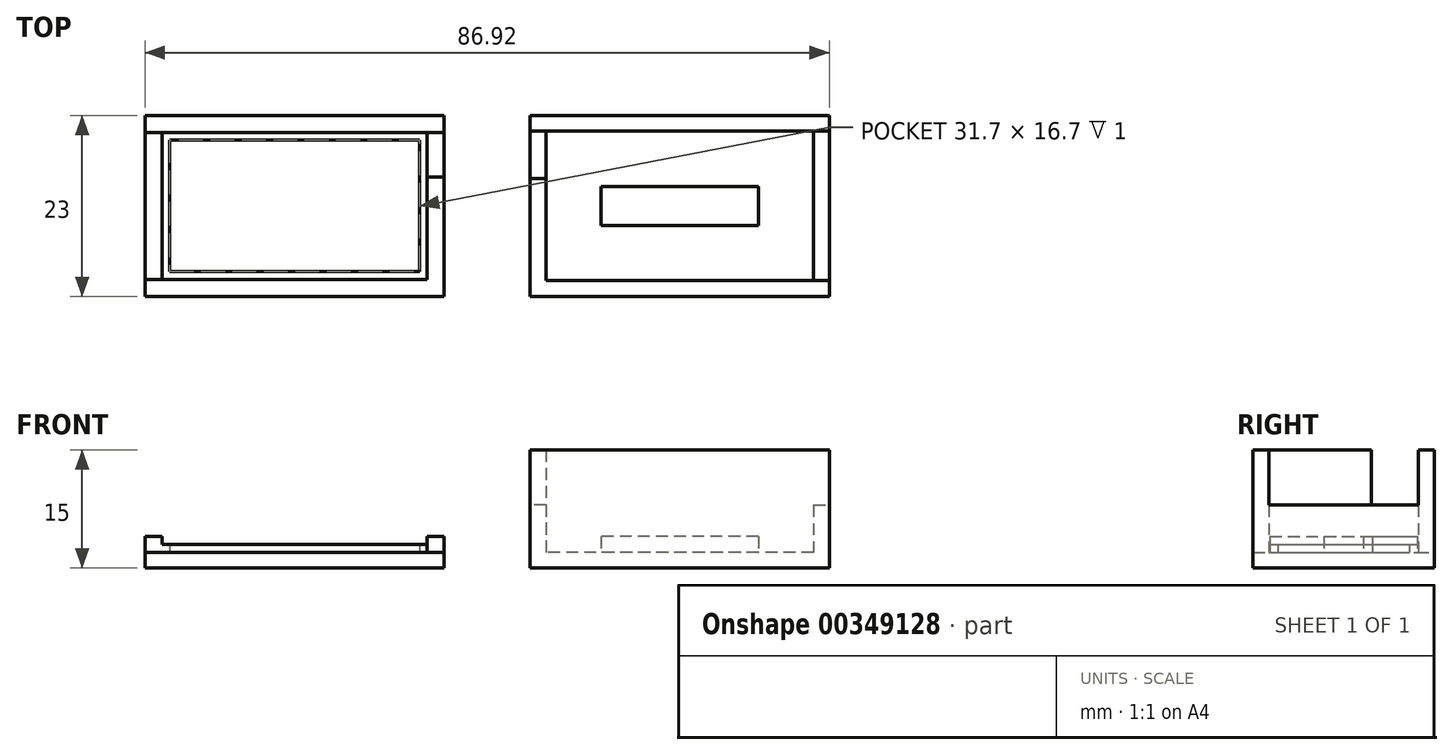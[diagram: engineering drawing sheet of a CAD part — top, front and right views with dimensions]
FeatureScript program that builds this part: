
annotation { "Feature Type Name" : "Feature", "Feature Type Description" : "" }
export const myFeature = defineFeature(function(context is Context, id is Id, definition is map)
    precondition{}
    {
        {
            var Q0;
            Q0=qCreatedBy(makeId("Top.planeOp"),FACE);
            var sketch = newSketch(context, id + "F0", { "sketchPlane" : qUnion([Q0])});
            skLineSegment(sketch, "E0.bottom", {"start": v(17, -9.5) * mm, "end": v(-17, -9.5) * mm});
            skLineSegment(sketch, "E0.top", {"start": v(17, 9.5) * mm, "end": v(-17, 9.5) * mm});
            skLineSegment(sketch, "E0.left", {"start": v(17, -9.5) * mm, "end": v(17, 9.5) * mm});
            skLineSegment(sketch, "E0.right", {"start": v(-17, -9.5) * mm, "end": v(-17, 9.5) * mm});
            skPoint(sketch, "E0.middle", {"position": v(0, 0) * mm});
            skLineSegment(sketch, "E1.bottom", {"start": v(10, -2.5) * mm, "end": v(-10, -2.5) * mm});
            skLineSegment(sketch, "E1.top", {"start": v(10, 2.5) * mm, "end": v(-10, 2.5) * mm});
            skLineSegment(sketch, "E1.left", {"start": v(10, -2.5) * mm, "end": v(10, 2.5) * mm});
            skLineSegment(sketch, "E1.right", {"start": v(-10, -2.5) * mm, "end": v(-10, 2.5) * mm});
            skLineSegment(sketch, "E2.0", {"start": v(19, 11.5) * mm, "end": v(-19, 11.5) * mm});
            skLineSegment(sketch, "E2.1", {"start": v(19, -11.5) * mm, "end": v(19, 11.5) * mm});
            skLineSegment(sketch, "E2.2", {"start": v(19, -11.5) * mm, "end": v(-19, -11.5) * mm});
            skLineSegment(sketch, "E2.3", {"start": v(-19, -11.5) * mm, "end": v(-19, 11.5) * mm});
            skLineSegment(sketch, "E3", {"start": v(17, 9.5) * mm, "end": v(19, 9.5) * mm});
            skLineSegment(sketch, "E4", {"start": v(17, -9.5) * mm, "end": v(19, -9.5) * mm});
            skLineSegment(sketch, "E5", {"start": v(-17, 9.5) * mm, "end": v(-19, 9.5) * mm});
            skLineSegment(sketch, "E6", {"start": v(-17, 3.5) * mm, "end": v(-19, 3.5) * mm});
            skSolve(sketch);
        }
        {
            var Q0;
            Q0=makeQuery(id+"F0.imprint","IMPRINT",FACE,{"disambiguationData":[TD([[makeQuery(id+"F0.imprint","IMPRINT",EDGE,{"derivedFrom":sQuery(id+"F0.wireOp",EDGE,"E0.bottom")}),-1.0]])]});
            extrude(context, id + "F1", {"entities" : qUnion([Q0]), "depth" : 2 * mm});
        }
        {
            var Q0;
            Q0=makeQuery(id+"F0.imprint","IMPRINT",FACE,{"disambiguationData":[TD([[makeQuery(id+"F0.imprint","IMPRINT",EDGE,{"derivedFrom":sQuery(id+"F0.wireOp",EDGE,"E1.bottom")}),-1.0]])]});
            extrude(context, id + "F2", {"entities" : qUnion([Q0]), "operationType" : NewBodyOperationType.ADD, "depth" : 4 * mm});
        }
        {
            var Q0;
            Q0=makeQuery(id+"F0.imprint","IMPRINT",FACE,{"disambiguationData":[TD([[makeQuery(id+"F0.imprint","IMPRINT",EDGE,{"derivedFrom":sQuery(id+"F0.wireOp",EDGE,"E0.bottom")}),1.0]])]});
            var Q1;
            Q1=makeQuery(id+"F0.imprint","IMPRINT",FACE,{"disambiguationData":[TD([[makeQuery(id+"F0.imprint","IMPRINT",EDGE,{"derivedFrom":sQuery(id+"F0.wireOp",EDGE,"E0.top")}),-1.0]])]});
            extrude(context, id + "F3", {"entities" : qUnion([Q0, Q1]), "operationType" : NewBodyOperationType.ADD, "depth" : 15 * mm});
        }
        {
            var Q0;
            Q0=makeQuery(id+"F0.imprint","IMPRINT",FACE,{"disambiguationData":[TD([[makeQuery(id+"F0.imprint","IMPRINT",EDGE,{"derivedFrom":sQuery(id+"F0.wireOp",EDGE,"E0.left")}),-1.0]])]});
            var Q1;
            {var subQ0=sQuery(id+"F0.wireOp",EDGE,"E5");Q1=makeQuery(id+"F0.imprint","IMPRINT",FACE,{"disambiguationData":[TD([[makeQuery(id+"F0.imprint","IMPRINT",EDGE,{"derivedFrom":subQ0}),1.0]])]});}
            extrude(context, id + "F4", {"entities" : qUnion([Q0, Q1]), "operationType" : NewBodyOperationType.ADD, "depth" : 8 * mm});
        }
        {
            var Q0;
            Q0=qCreatedBy(makeId("Top.planeOp"),FACE);
            var sketch = newSketch(context, id + "F5", { "sketchPlane" : qUnion([Q0])});
            skLineSegment(sketch, "E7.bottom", {"start": v(-32.07, -9.35) * mm, "end": v(-65.77, -9.35) * mm});
            skLineSegment(sketch, "E7.top", {"start": v(-32.07, 9.35) * mm, "end": v(-65.77, 9.35) * mm});
            skLineSegment(sketch, "E7.left", {"start": v(-32.07, -9.35) * mm, "end": v(-32.07, 9.35) * mm});
            skLineSegment(sketch, "E7.right", {"start": v(-65.77, -9.35) * mm, "end": v(-65.77, 9.35) * mm});
            skPoint(sketch, "E7.middle", {"position": v(-48.92, 0) * mm});
            skLineSegment(sketch, "E8.0", {"start": v(-29.92, 11.5) * mm, "end": v(-67.92, 11.5) * mm});
            skLineSegment(sketch, "E8.1", {"start": v(-29.92, -11.5) * mm, "end": v(-29.92, 11.5) * mm});
            skLineSegment(sketch, "E8.2", {"start": v(-29.92, -11.5) * mm, "end": v(-67.92, -11.5) * mm});
            skLineSegment(sketch, "E8.3", {"start": v(-67.92, -11.5) * mm, "end": v(-67.92, 11.5) * mm});
            skLineSegment(sketch, "E9", {"start": v(-32.07, 9.35) * mm, "end": v(-29.92, 9.35) * mm});
            skLineSegment(sketch, "E10", {"start": v(-32.07, -9.35) * mm, "end": v(-29.92, -9.35) * mm});
            skLineSegment(sketch, "E11", {"start": v(-29.92, 3.65) * mm, "end": v(-32.07, 3.65) * mm});
            skLineSegment(sketch, "E12", {"start": v(-65.77, 9.35) * mm, "end": v(-67.92, 9.35) * mm});
            skLineSegment(sketch, "E13", {"start": v(-65.77, -9.35) * mm, "end": v(-67.92, -9.35) * mm});
            skLineSegment(sketch, "E14.0", {"start": v(-33.07, 8.35) * mm, "end": v(-64.77, 8.35) * mm});
            skLineSegment(sketch, "E14.1", {"start": v(-33.07, -8.35) * mm, "end": v(-33.07, 8.35) * mm});
            skLineSegment(sketch, "E14.2", {"start": v(-33.07, -8.35) * mm, "end": v(-64.77, -8.35) * mm});
            skLineSegment(sketch, "E14.3", {"start": v(-64.77, -8.35) * mm, "end": v(-64.77, 8.35) * mm});
            skSolve(sketch);
        }
        {
            var Q0;
            Q0=makeQuery(id+"F5.imprint","IMPRINT",FACE,{"disambiguationData":[TD([[makeQuery(id+"F5.imprint","IMPRINT",EDGE,{"derivedFrom":sQuery(id+"F5.wireOp",EDGE,"E7.top")}),-1.0]])]});
            var Q1;
            Q1=makeQuery(id+"F5.imprint","IMPRINT",FACE,{"disambiguationData":[TD([[makeQuery(id+"F5.imprint","IMPRINT",EDGE,{"derivedFrom":sQuery(id+"F5.wireOp",EDGE,"E7.bottom")}),1.0]])]});
            var Q2;
            {var subQ0=sQuery(id+"F5.wireOp",EDGE,"E10");Q2=makeQuery(id+"F5.imprint","IMPRINT",FACE,{"disambiguationData":[TD([[makeQuery(id+"F5.imprint","IMPRINT",EDGE,{"derivedFrom":subQ0}),1.0]])]});}
            var Q3;
            Q3=makeQuery(id+"F5.imprint","IMPRINT",FACE,{"disambiguationData":[TD([[makeQuery(id+"F5.imprint","IMPRINT",EDGE,{"derivedFrom":sQuery(id+"F5.wireOp",EDGE,"E14.0")}),1.0]])]});
            extrude(context, id + "F6", {"entities" : qUnion([Q0, Q1, Q2, Q3]), "depth" : 2 * mm});
        }
        {
            var Q0;
            {var subQ3=sQuery(id+"F5.wireOp",EDGE,"E7.bottom");Q0=makeQuery(id+"F5.imprint","IMPRINT",FACE,{"disambiguationData":[TD([[makeQuery(id+"F5.imprint","IMPRINT",EDGE,{"derivedFrom":subQ3}),-1.0]])]});}
            extrude(context, id + "F7", {"entities" : qUnion([Q0]), "operationType" : NewBodyOperationType.ADD, "depth" : 3 * mm});
        }
        {
            var Q0;
            {var subQ0=sQuery(id+"F5.wireOp",EDGE,"E9");Q0=makeQuery(id+"F5.imprint","IMPRINT",FACE,{"disambiguationData":[TD([[makeQuery(id+"F5.imprint","IMPRINT",EDGE,{"derivedFrom":subQ0}),-1.0]])]});}
            var Q1;
            Q1=makeQuery(id+"F5.imprint","IMPRINT",FACE,{"disambiguationData":[TD([[makeQuery(id+"F5.imprint","IMPRINT",EDGE,{"derivedFrom":sQuery(id+"F5.wireOp",EDGE,"E7.right")}),1.0]])]});
            extrude(context, id + "F8", {"entities" : qUnion([Q0, Q1]), "operationType" : NewBodyOperationType.ADD, "depth" : 4 * mm});
        }
    });
